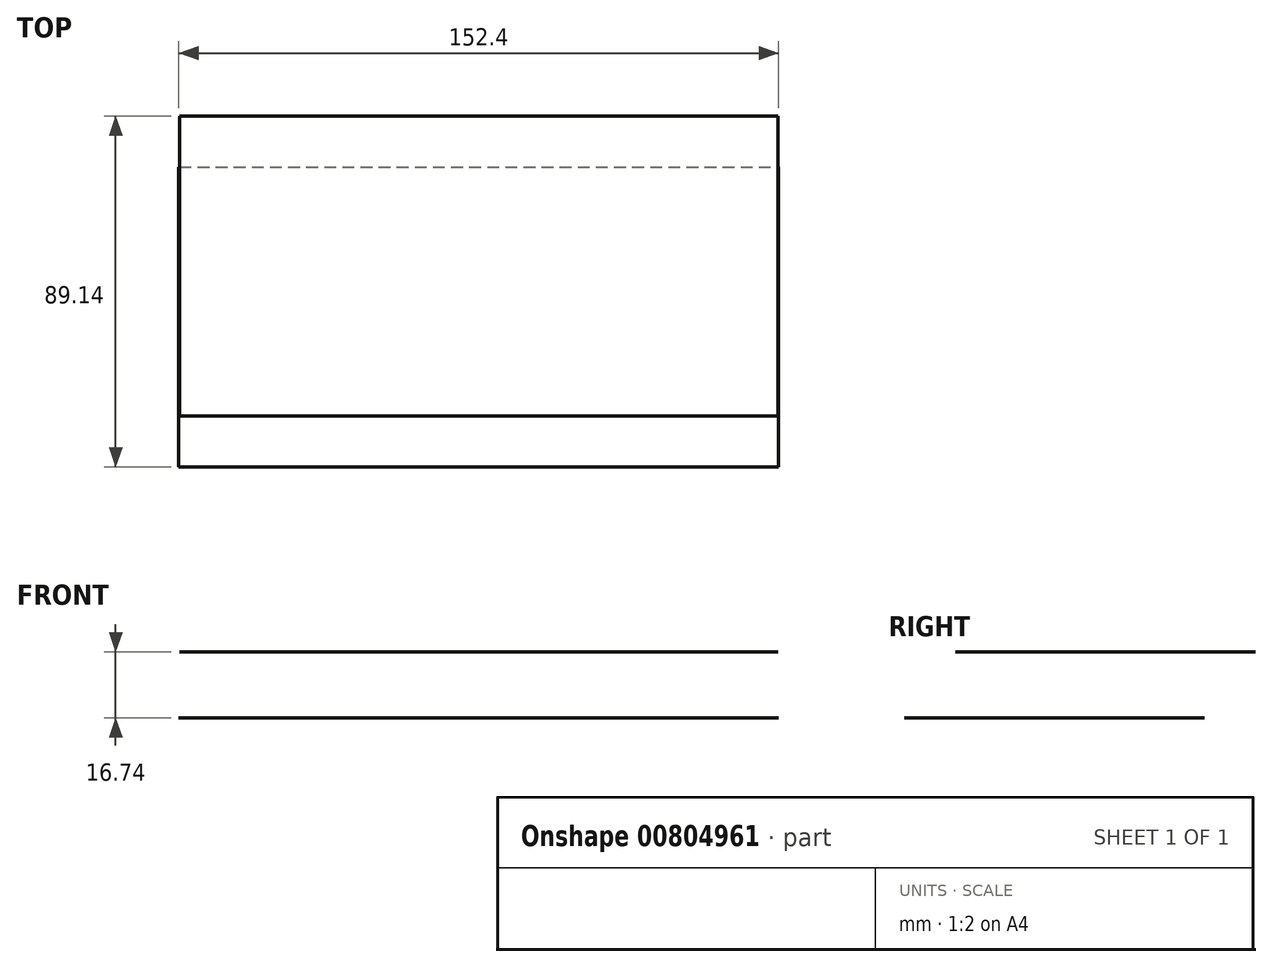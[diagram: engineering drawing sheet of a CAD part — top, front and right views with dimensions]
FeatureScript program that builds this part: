
annotation { "Feature Type Name" : "Feature", "Feature Type Description" : "" }
export const myFeature = defineFeature(function(context is Context, id is Id, definition is map)
    precondition{}
    {
        {
            var Q0;
            Q0=qCreatedBy(makeId("Top.planeOp"),FACE);
            var sketch = newSketch(context, id + "F0", { "sketchPlane" : qUnion([Q0])});
            skLineSegment(sketch, "E0.bottom", {"start": v(-76.2, 12.94) * mm, "end": v(76.2, 12.94) * mm});
            skLineSegment(sketch, "E0.top", {"start": v(-76.2, -12.94) * mm, "end": v(76.2, -12.94) * mm});
            skLineSegment(sketch, "E0.left", {"start": v(-76.2, 12.94) * mm, "end": v(-76.2, -12.94) * mm});
            skLineSegment(sketch, "E0.right", {"start": v(76.2, 12.94) * mm, "end": v(76.2, -12.94) * mm});
            skPoint(sketch, "E0.middle", {"position": v(0, 0) * mm});
            skArc(sketch, "E1", {"start": v(89.14, 0) * mm, "mid": v(85.35, 9.16) * mm, "end": v(76.19, 12.94) * mm});
            skPoint(sketch, "E1.startSnap0", {"position": v(76.2, 0) * mm});
            skArc(sketch, "E2", {"start": v(76.2, -12.94) * mm, "mid": v(85.35, -9.15) * mm, "end": v(89.14, 0) * mm});
            skArc(sketch, "E3", {"start": v(-76.2, 12.94) * mm, "mid": v(-89.14, 0) * mm, "end": v(-76.2, -12.94) * mm});
            skSolve(sketch);
        }
        {
            var Q0;
            Q0=qCreatedBy(makeId("Front.planeOp"),FACE);
            var sketch = newSketch(context, id + "F1", { "sketchPlane" : qUnion([Q0])});
            skLineSegment(sketch, "E4.bottom", {"start": v(-76.01, 16.74) * mm, "end": v(76.01, 16.74) * mm});
            skLineSegment(sketch, "E4.top", {"start": v(-76.01, -16.74) * mm, "end": v(76.01, -16.74) * mm});
            skLineSegment(sketch, "E4.left", {"start": v(-76.01, 16.74) * mm, "end": v(-76.01, -16.74) * mm});
            skLineSegment(sketch, "E4.right", {"start": v(76.01, 16.74) * mm, "end": v(76.01, -16.74) * mm});
            skPoint(sketch, "E4.middle", {"position": v(0, 0) * mm});
            skSolve(sketch);
        }
        {
            var Q0;
            Q0=sQuery(id+"F1.wireOp",EDGE,"E4.bottom");
            var Q1;
            Q1=sQuery(id+"F0.wireOp",EDGE,"E0.top");
            extrude(context, id + "F2", {"bodyType" : ToolBodyType.SURFACE, "surfaceEntities" : qUnion([Q0, Q1]), "depth" : 76.2 * mm, "offsetDistance" : 25.4 * mm});
        }
    });
